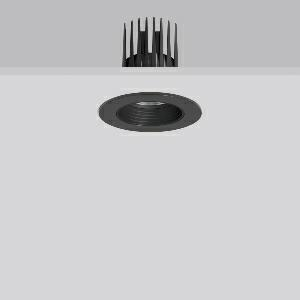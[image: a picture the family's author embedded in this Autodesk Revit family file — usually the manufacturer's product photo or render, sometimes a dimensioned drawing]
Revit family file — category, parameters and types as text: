
# Revit family: heledon_mini_e_901753_003_3_f301
name_source: partatom
category: Lighting Fixtures
units: mm (PartAtom-declared; Revit-internal decimal feet)

## family parameters
Cut with Voids When Loaded = No
Host = Face
Light Source = No
Part Type = Normal
Room Calculation Point = No
Round Connector Dimension = Use Diameter
Shared = No

## types (1)
- HELEDON mini E (1 x LED Modul 935, 2900 lm, 3500)
    Apparent Load = 29 VA
    Approval mark = CE
    CIE Flux Codes = 98 100 100 100 100
    Color Rendering = 92
    Color Temperature = 3500
    Default Elevation = 1800 mm
    Description = Series: HELEDON mini
Round recessed downlight. Housing: die-cast aluminium, powder-coated. Black plastic ring and recessed LED to prevent glare from the side. Optical assembly with lens made of plastic (polycarbonate) for the best homogeneous light distribution - can be changed without tools. Best colour rendering index Ra>90. Suitable for Recessed ceiling mounting. Installation without tools thanks to spring fastening system. Including separate LED converter with connecting cable 600 mm.High quality converter without flickering and stroboscopic effect. Through-wiring box (5 pole) available as accessory. The following accessories can be mounted without use of tools: interchangeable lenses, decorative glasses, honeycomb louvre, clear and frosted diffusers, white interchangeable plastic ring. 
Colour: deep black, matt (RAL 9005)
Diameter: 124 mm
Height: 3 mm
Cut-out diameter: 114 mm
Recess height: 170 mm
Luminaire: recess height: 120 mm
Lamp: LED
Socket: without socket
Colour temperature: 3500K
Colour rendering index (CRI): 92
System power: 29 W
Rated luminous flux: 2900 lm
Luminous efficiency: 100 lm/W
Control gear: Regulated power supply
Protection class: II
Type of protection: IP 20
    Height = 0 mm  [stored 0 ft]
    Lamp = 1 x LED Modul 935
    Lamp Light Flux = 2900 lm
    Lamp count = 1
    Length = 124 mm  [stored 0.406824 ft]
    Lifetime = 50000 h
    Luminous efficacy = 100 lm/W
    Manufacturer = RZB
    ModVariant = No
    Model = 901753.003.3
    Mounting Place = Ceiling
    Mounting Type = Recessed
    Number of Poles = 1
    OnlyDefault = Yes
    Power Factor = 1
    Product Name = HELEDON mini E
    Product group = Recessed downlights
    ProductGroupID = 402
    Protection Class = Protection class II
    Protection Degree = IP 20
    RLX_Detail_Level = 1
    RLX_Emergency_Light_Flux = 0 lm
    RLX_Emergency_Type = 0
    RLX_Emergency_Type_DB = No
    RlxData = <blob elided: 128241 chars, md5=2b6fb0c2>
    Socket = socket
    Standby Power = 0 W
    System Light Flux = 2900 lm
    System Power = 29 W
    Type Comments = Product without accessories
    Type Image = 901656.003.jpg
    URL = http://relux.com
    VarID = ---
    Voltage = 230 V
    Voltage Range = 220-240 V
    Weight = 0.00 kg
    Width = 0 mm  [stored 0 ft]

note: [stored X ft] marks values corroborated as IEEE doubles in the binary element streams (Revit-internal decimal feet)

## geometry (parser evidence)
native form markers: Blend x4, Sweep x11
no freeform markers — native parametric forms only
